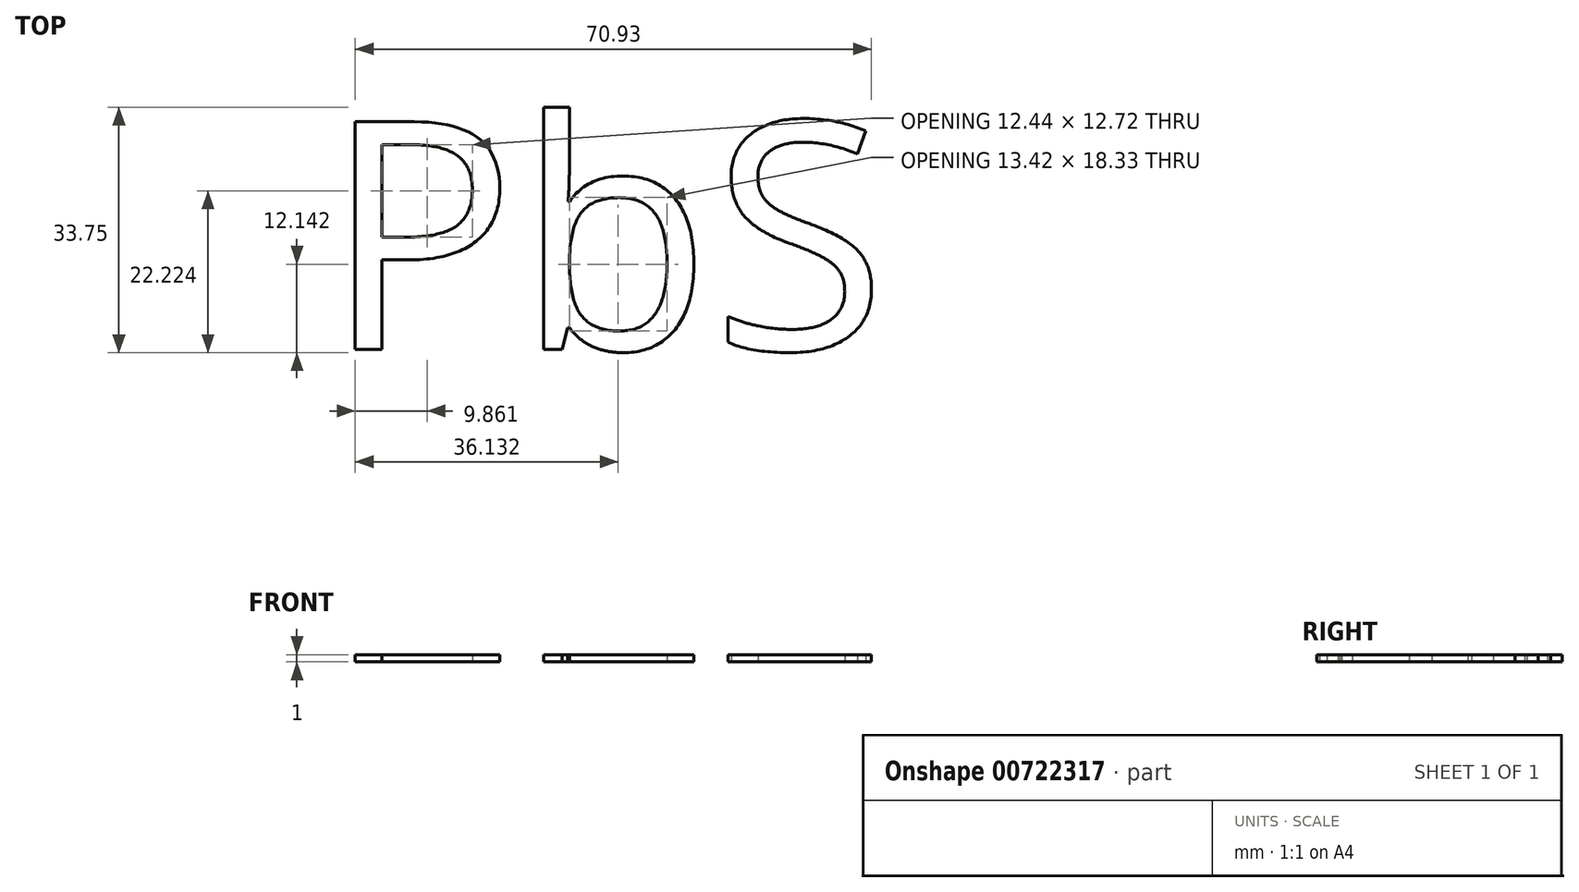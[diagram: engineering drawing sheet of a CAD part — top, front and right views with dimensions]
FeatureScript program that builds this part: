
annotation { "Feature Type Name" : "Feature", "Feature Type Description" : "" }
export const myFeature = defineFeature(function(context is Context, id is Id, definition is map)
    precondition{}
    {
        {
            var Q0;
            Q0=qCreatedBy(makeId("Top.planeOp"),FACE);
            var sketch = newSketch(context, id + "F0", { "sketchPlane" : qUnion([Q0])});
            skText(sketch, "E0", { "text": "PbS", "fontName": "OpenSans-Regular.ttf"});
            const initialGuessF0  = {"E0": [-0.04148, -0.01277, 1, 0, 0.03157]};
            skSetInitialGuess(sketch, initialGuessF0);
            skSolve(sketch);
        }
        {
            var Q0;
            Q0 = qSketchRegion(id + "F0", true);
            extrude(context, id + "F1", {"entities" : qUnion([Q0]), "depth" : 1 * mm, "offsetDistance" : 25 * mm});
        }
    });
